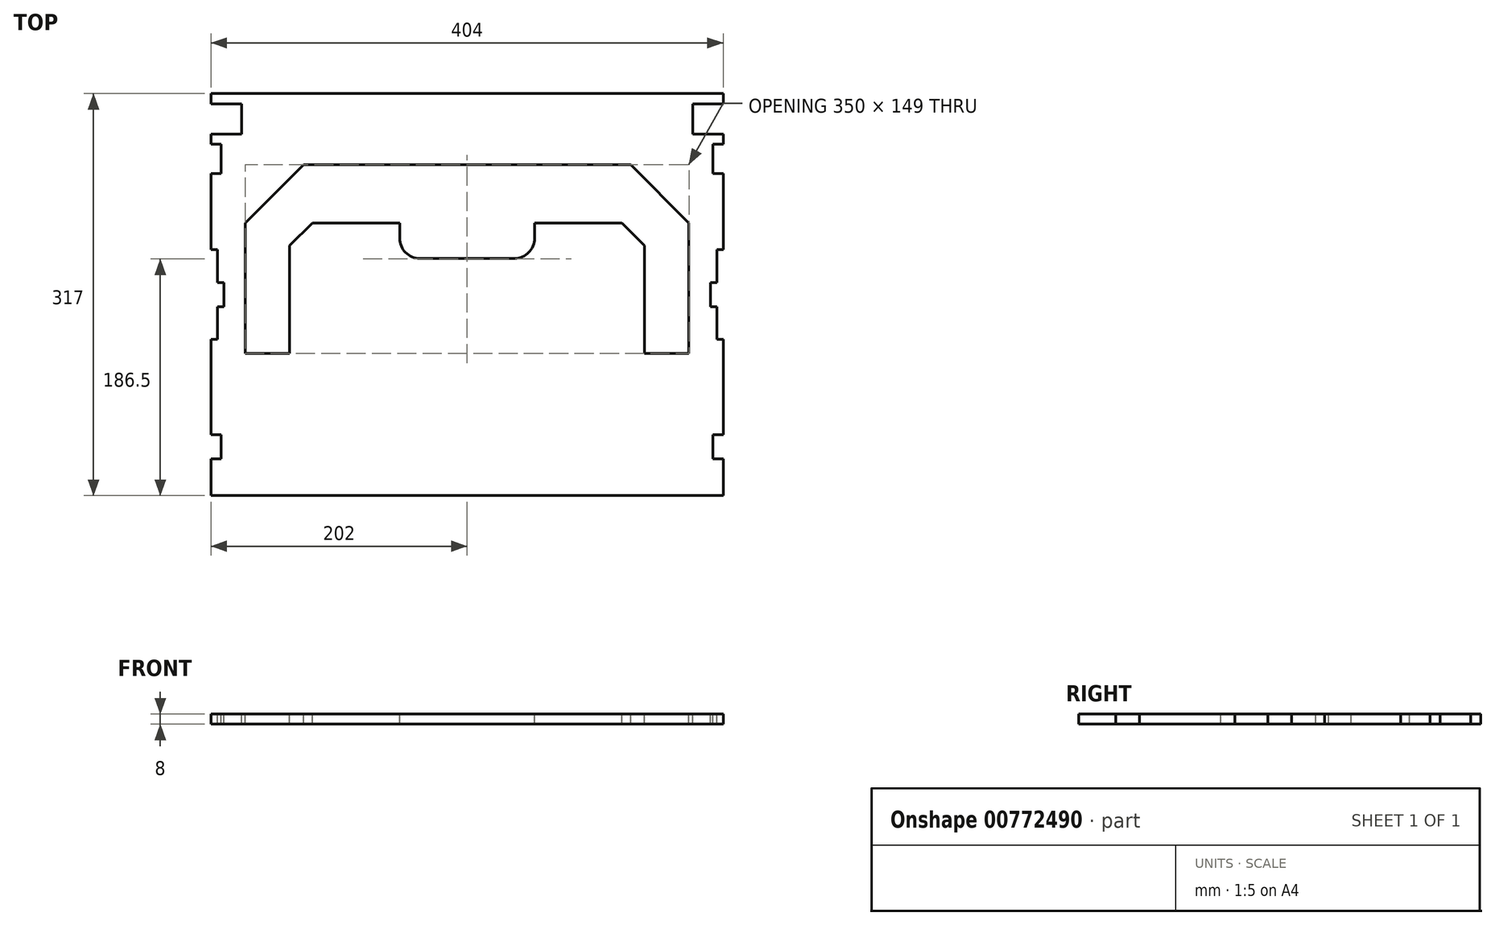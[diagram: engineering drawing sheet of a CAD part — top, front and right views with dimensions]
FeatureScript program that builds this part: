
annotation { "Feature Type Name" : "Feature", "Feature Type Description" : "" }
export const myFeature = defineFeature(function(context is Context, id is Id, definition is map)
    precondition{}
    {
        {
            var Q0;
            Q0=qCreatedBy(makeId("Top.planeOp"),FACE);
            var sketch = newSketch(context, id + "F0", { "sketchPlane" : qUnion([Q0])});
            skLineSegment(sketch, "E0.bottom", {"start": v(202, -158.5) * mm, "end": v(-202, -158.5) * mm});
            skLineSegment(sketch, "E0.top", {"start": v(202, 158.5) * mm, "end": v(-202, 158.5) * mm});
            skLineSegment(sketch, "E0.left", {"start": v(202, -158.5) * mm, "end": v(202, 158.5) * mm});
            skLineSegment(sketch, "E0.right", {"start": v(-202, -158.5) * mm, "end": v(-202, 158.5) * mm});
            skPoint(sketch, "E0.middle", {"position": v(0, 0) * mm});
            skSolve(sketch);
        }
        {
            var Q0;
            Q0=makeQuery(id+"F0.imprint","IMPRINT",FACE,{"disambiguationData":[TD([[makeQuery(id+"F0.imprint","IMPRINT",EDGE,{"derivedFrom":sQuery(id+"F0.wireOp",EDGE,"E0.bottom")}),-1.0]])]});
            extrude(context, id + "F1", {"entities" : qUnion([Q0]), "depth" : 8 * mm, "offsetDistance" : 25 * mm});
        }
        {
            var Q0;
            Q0=makeQuery(id+"F1.opExtrude","CAP_FACE",FACE,{"disambiguationData":[OSD([sQuery(id+"F0.wireOp",EDGE,"E0.bottom"),sQuery(id+"F0.wireOp",EDGE,"E0.top"),sQuery(id+"F0.wireOp",EDGE,"E0.left"),sQuery(id+"F0.wireOp",EDGE,"E0.right")])],"isStart":false});
            var sketch = newSketch(context, id + "F2", { "sketchPlane" : qUnion([Q0])});
            skLineSegment(sketch, "E1.bottom", {"start": v(-202, -129.5) * mm, "end": v(-194, -129.5) * mm});
            skLineSegment(sketch, "E1.top", {"start": v(-202, -110.5) * mm, "end": v(-194, -110.5) * mm});
            skLineSegment(sketch, "E1.left", {"start": v(-202, -129.5) * mm, "end": v(-202, -110.5) * mm});
            skLineSegment(sketch, "E1.right", {"start": v(-194, -129.5) * mm, "end": v(-194, -110.5) * mm});
            skLineSegment(sketch, "E2", {"start": v(-202, -35.5) * mm, "end": v(-197, -35.5) * mm});
            skLineSegment(sketch, "E3", {"start": v(-197, -35.5) * mm, "end": v(-197, -9.5) * mm});
            skLineSegment(sketch, "E4", {"start": v(-197, -9.5) * mm, "end": v(-192, -9.5) * mm});
            skLineSegment(sketch, "E5", {"start": v(-192, 9.5) * mm, "end": v(-197, 9.5) * mm});
            skLineSegment(sketch, "E6", {"start": v(-197, 9.5) * mm, "end": v(-197, 35.5) * mm});
            skLineSegment(sketch, "E7", {"start": v(-197, 35.5) * mm, "end": v(-202, 35.5) * mm});
            skLineSegment(sketch, "E8", {"start": v(-202, 35.5) * mm, "end": v(-202, -35.5) * mm});
            skLineSegment(sketch, "E9", {"start": v(-192, 9.5) * mm, "end": v(-192, -9.5) * mm});
            skLineSegment(sketch, "E10.bottom", {"start": v(-202, 95.5) * mm, "end": v(-194, 95.5) * mm});
            skLineSegment(sketch, "E10.top", {"start": v(-202, 118.5) * mm, "end": v(-194, 118.5) * mm});
            skLineSegment(sketch, "E10.left", {"start": v(-202, 95.5) * mm, "end": v(-202, 118.5) * mm});
            skLineSegment(sketch, "E10.right", {"start": v(-194, 95.5) * mm, "end": v(-194, 118.5) * mm});
            skLineSegment(sketch, "E11.bottom", {"start": v(-202, 150.5) * mm, "end": v(-178, 150.5) * mm});
            skLineSegment(sketch, "E11.top", {"start": v(-202, 126.5) * mm, "end": v(-178, 126.5) * mm});
            skLineSegment(sketch, "E11.left", {"start": v(-202, 150.5) * mm, "end": v(-202, 126.5) * mm});
            skLineSegment(sketch, "E11.right", {"start": v(-178, 150.5) * mm, "end": v(-178, 126.5) * mm});
            skLineSegment(sketch, "E12.MirrorCS", {"start": v(197, -9.5) * mm, "end": v(192, -9.5) * mm});
            skLineSegment(sketch, "E13.MirrorCS", {"start": v(202, -35.5) * mm, "end": v(197, -35.5) * mm});
            skLineSegment(sketch, "E14.MirrorCS", {"start": v(202, -110.5) * mm, "end": v(194, -110.5) * mm});
            skLineSegment(sketch, "E15.MirrorCS", {"start": v(202, -129.5) * mm, "end": v(194, -129.5) * mm});
            skLineSegment(sketch, "E16.MirrorCS", {"start": v(192, 9.5) * mm, "end": v(197, 9.5) * mm});
            skLineSegment(sketch, "E17.MirrorCS", {"start": v(197, 35.5) * mm, "end": v(202, 35.5) * mm});
            skLineSegment(sketch, "E18.MirrorCS", {"start": v(202, 118.5) * mm, "end": v(194, 118.5) * mm});
            skLineSegment(sketch, "E19.MirrorCS", {"start": v(202, 95.5) * mm, "end": v(194, 95.5) * mm});
            skLineSegment(sketch, "E20.MirrorCS", {"start": v(197, -35.5) * mm, "end": v(197, -9.5) * mm});
            skLineSegment(sketch, "E21.MirrorCS", {"start": v(194, -129.5) * mm, "end": v(194, -110.5) * mm});
            skLineSegment(sketch, "E22.MirrorCS", {"start": v(202, -129.5) * mm, "end": v(202, -110.5) * mm});
            skLineSegment(sketch, "E23.MirrorCS", {"start": v(197, 9.5) * mm, "end": v(197, 35.5) * mm});
            skLineSegment(sketch, "E24.MirrorCS", {"start": v(202, 150.5) * mm, "end": v(202, 126.5) * mm});
            skLineSegment(sketch, "E25.MirrorCS", {"start": v(202, 95.5) * mm, "end": v(202, 118.5) * mm});
            skLineSegment(sketch, "E26.MirrorCS", {"start": v(202, 126.5) * mm, "end": v(178, 126.5) * mm});
            skLineSegment(sketch, "E27.MirrorCS", {"start": v(202, 35.5) * mm, "end": v(202, -35.5) * mm});
            skLineSegment(sketch, "E28.MirrorCS", {"start": v(194, 95.5) * mm, "end": v(194, 118.5) * mm});
            skLineSegment(sketch, "E29.MirrorCS", {"start": v(202, 150.5) * mm, "end": v(178, 150.5) * mm});
            skLineSegment(sketch, "E30.MirrorCS", {"start": v(192, 9.5) * mm, "end": v(192, -9.5) * mm});
            skLineSegment(sketch, "E31.MirrorCS", {"start": v(178, 150.5) * mm, "end": v(178, 126.5) * mm});
            skSolve(sketch);
        }
        {
            var Q0;
            Q0 = qSketchRegion(id + "F2", true);
            extrude(context, id + "F3", {"entities" : qUnion([Q0]), "operationType" : NewBodyOperationType.REMOVE, "oppositeDirection" : true, "depth" : 8 * mm, "offsetDistance" : 25 * mm});
        }
        {
            var Q0;
            Q0=makeQuery(id+"F1.opExtrude","CAP_FACE",FACE,{"disambiguationData":[OSD([sQuery(id+"F0.wireOp",EDGE,"E0.bottom"),sQuery(id+"F0.wireOp",EDGE,"E0.top"),sQuery(id+"F0.wireOp",EDGE,"E0.left"),sQuery(id+"F0.wireOp",EDGE,"E0.right")])],"isStart":false});
            var sketch = newSketch(context, id + "F4", { "sketchPlane" : qUnion([Q0])});
            skLineSegment(sketch, "E32", {"start": v(-175, -46.5) * mm, "end": v(-175, 56.5) * mm});
            skLineSegment(sketch, "E33", {"start": v(-175, 56.5) * mm, "end": v(-129, 102.5) * mm});
            skLineSegment(sketch, "E34", {"start": v(-129, 102.5) * mm, "end": v(129, 102.5) * mm});
            skLineSegment(sketch, "E35", {"start": v(129, 102.5) * mm, "end": v(175, 56.5) * mm});
            skLineSegment(sketch, "E36", {"start": v(175, 56.5) * mm, "end": v(175, -46.5) * mm});
            skLineSegment(sketch, "E37", {"start": v(175, -46.5) * mm, "end": v(140, -46.5) * mm});
            skLineSegment(sketch, "E38", {"start": v(140, -46.5) * mm, "end": v(140, 38.5) * mm});
            skLineSegment(sketch, "E39", {"start": v(140, 38.5) * mm, "end": v(122, 56.5) * mm});
            skLineSegment(sketch, "E40", {"start": v(122, 56.5) * mm, "end": v(53.22, 56.5) * mm});
            skLineSegment(sketch, "E41", {"start": v(-122, 56.5) * mm, "end": v(-140, 38.5) * mm});
            skLineSegment(sketch, "E42", {"start": v(-140, 38.5) * mm, "end": v(-140, -46.5) * mm});
            skLineSegment(sketch, "E43", {"start": v(-140, -46.5) * mm, "end": v(-175, -46.5) * mm});
            skLineSegment(sketch, "E44.bottom", {"start": v(37.22, 28.5) * mm, "end": v(-37.22, 28.5) * mm});
            skLineSegment(sketch, "E44.left", {"start": v(53.22, 44.5) * mm, "end": v(53.22, 56.5) * mm});
            skLineSegment(sketch, "E44.right", {"start": v(-53.22, 44.5) * mm, "end": v(-53.22, 56.5) * mm});
            skLineSegment(sketch, "E45.trimOffspring", {"start": v(-53.22, 56.5) * mm, "end": v(-122, 56.5) * mm});
            skPoint(sketch, "E46.visualSharp", {"position": v(-53.22, 28.5) * mm});
            skArc(sketch, "E46.filletArc", {"start": v(-53.22, 44.5) * mm, "mid": v(-48.53, 33.19) * mm, "end": v(-37.22, 28.5) * mm});
            skPoint(sketch, "E47.visualSharp", {"position": v(53.22, 28.5) * mm});
            skArc(sketch, "E47.filletArc", {"start": v(37.22, 28.5) * mm, "mid": v(48.53, 33.19) * mm, "end": v(53.22, 44.5) * mm});
            skSolve(sketch);
        }
        {
            var Q0;
            Q0=makeQuery(id+"F4.imprint","IMPRINT",FACE,{"disambiguationData":[TD([[makeQuery(id+"F4.imprint","IMPRINT",EDGE,{"derivedFrom":sQuery(id+"F4.wireOp",EDGE,"E32")}),-1.0]])]});
            extrude(context, id + "F5", {"entities" : qUnion([Q0]), "operationType" : NewBodyOperationType.REMOVE, "endBound" : BoundingType.THROUGH_ALL, "oppositeDirection" : true, "depth" : 25 * mm, "offsetDistance" : 25 * mm});
        }
    });
